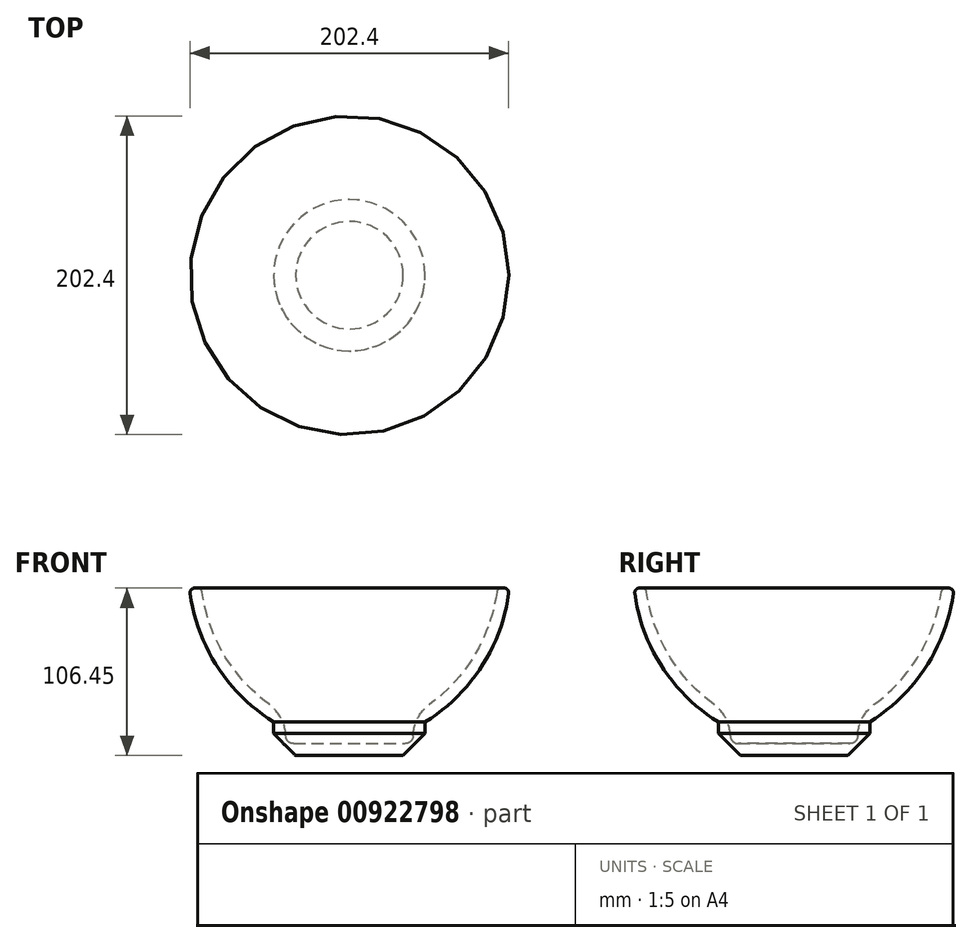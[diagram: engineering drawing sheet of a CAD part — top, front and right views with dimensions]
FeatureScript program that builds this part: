
annotation { "Feature Type Name" : "Feature", "Feature Type Description" : "" }
export const myFeature = defineFeature(function(context is Context, id is Id, definition is map)
    precondition{}
    {
        {
            var Q0;
            Q0=qCreatedBy(makeId("Front.planeOp"),FACE);
            var sketch = newSketch(context, id + "F0", { "sketchPlane" : qUnion([Q0])});
            skLineSegment(sketch, "E0", {"start": v(0, 74.08) * mm, "end": v(101.6, 74.08) * mm});
            skLineSegment(sketch, "E1", {"start": v(0, 74.08) * mm, "end": v(0, -27.52) * mm});
            skArc(sketch, "E2", {"start": v(0, -27.52) * mm, "mid": v(68.72, 5.36) * mm, "end": v(101.6, 74.08) * mm});
            skLineSegment(sketch, "E3", {"start": v(48.07, -11) * mm, "end": v(48.07, -32.37) * mm});
            skLineSegment(sketch, "E4", {"start": v(48.07, -32.37) * mm, "end": v(0, -32.37) * mm});
            skLineSegment(sketch, "E5", {"start": v(0, -27.52) * mm, "end": v(0, -32.37) * mm});
            skSolve(sketch);
        }
        {
            var Q0;
            {var subQ2=sQuery(id+"F0.wireOp",EDGE,"E3");Q0=makeQuery(id+"F0.imprint","IMPRINT",FACE,{"disambiguationData":[TD([[makeQuery(id+"F0.imprint","IMPRINT",EDGE,{"derivedFrom":subQ2}),-1.0]])]});}
            var Q1;
            {var subQ0=sQuery(id+"F0.wireOp",EDGE,"E0");Q1=makeQuery(id+"F0.imprint","IMPRINT",FACE,{"disambiguationData":[TD([[makeQuery(id+"F0.imprint","IMPRINT",EDGE,{"derivedFrom":subQ0}),-1.0]])]});}
            var Q2;
            Q2=sQuery(id+"F0.wireOp",EDGE,"E1");
            revolve(context, id + "F1", {"surfaceOperationType" : NewSurfaceOperationType.NEW, "entities" : qUnion([Q0, Q1]), "axis" : qUnion([Q2]), "revolveType" : RevolveType.FULL});
        }
        {
            var Q0;
            Q0=makeQuery(id+"F1.opRevolve","SWEPT_FACE",FACE,{"disambiguationData":[OSD([sQuery(id+"F0.wireOp",EDGE,"E0")])]});
            shell(context, id + "F2", {"entities" : qUnion([Q0]), "thickness" : 7.62 * mm});
        }
        {
            var Q0;
            Q0=makeQuery(id+"F1.opRevolve","SWEPT_EDGE",EDGE,{"disambiguationData":[OSD([sQuery(id+"F0.wireOp",EDGE,"E3"),sQuery(id+"F0.wireOp",EDGE,"E4")])]});
            chamfer(context, id + "F3", {"entities" : qUnion([Q0]), "width" : 13.97 * mm, "tangentPropagation" : true});
        }
        {
            var Q0;
            Q0=makeQuery(id+"F1.opRevolve","SWEPT_EDGE",EDGE,{"disambiguationData":[OSD([sQuery(id+"F0.wireOp",EDGE,"E0"),sQuery(id+"F0.wireOp",EDGE,"E2")])]});
            var Q1;
            Q1=makeQuery(id+"F2.opShell","OFFSET_EDGE",EDGE,{"disambiguationData":[OSD([sQuery(id+"F0.wireOp",EDGE,"E0"),sQuery(id+"F0.wireOp",EDGE,"E2")])]});
            fillet(context, id + "F4", {"entities" : qUnion([Q0, Q1]), "radius" : 3.05 * mm, "tangentPropagation" : true, "allowEdgeOverflow" : false});
        }
        {
            var Q0;
            Q0=makeQuery(id+"F2.opShell","OFFSET_FACE",FACE,{"disambiguationData":[OSD([sQuery(id+"F0.wireOp",EDGE,"E2")])]});
            var Q1;
            Q1=makeQuery(id+"F2.opShell","OFFSET_EDGE",EDGE,{"disambiguationData":[OSD([sQuery(id+"F0.wireOp",EDGE,"E2"),sQuery(id+"F0.wireOp",EDGE,"E3")])]});
            fillet(context, id + "F5", {"entities" : qUnion([Q0, Q1]), "radius" : 25.4 * mm, "tangentPropagation" : true, "allowEdgeOverflow" : false});
        }
        {
            var Q0;
            Q0=makeQuery(id+"F2.opShell","OFFSET_EDGE",EDGE,{"disambiguationData":[OSD([sQuery(id+"F0.wireOp",EDGE,"E3"),sQuery(id+"F0.wireOp",EDGE,"E4")])]});
            fillet(context, id + "F6", {"entities" : qUnion([Q0]), "radius" : 5.08 * mm, "tangentPropagation" : true, "allowEdgeOverflow" : false});
        }
    });
